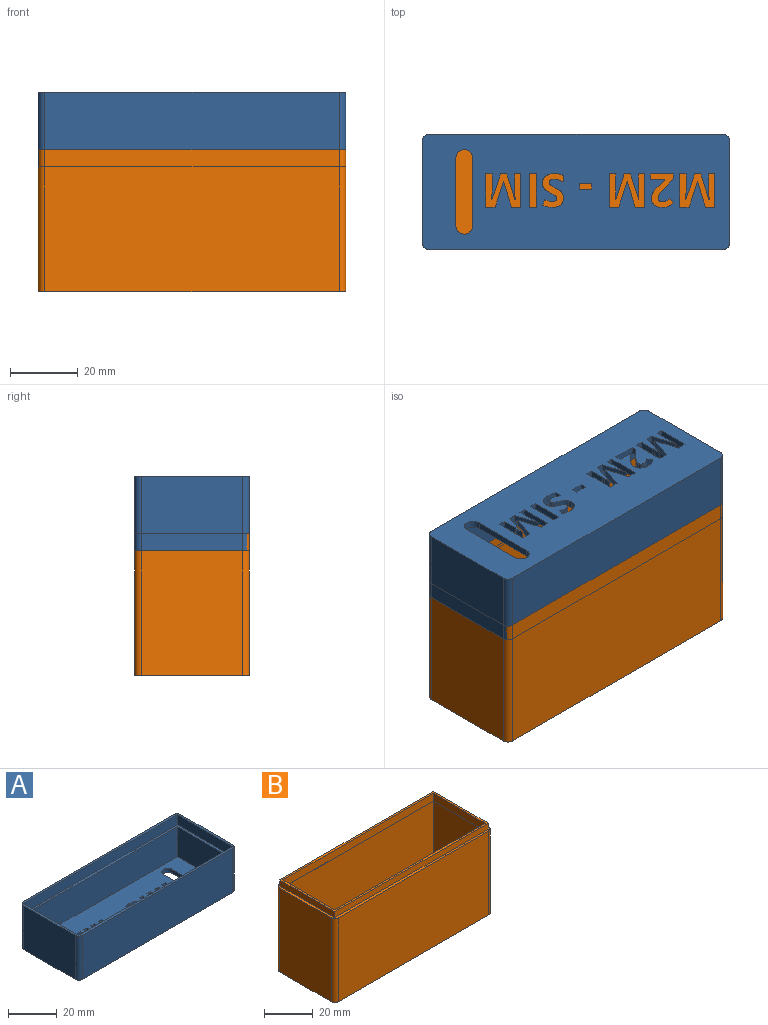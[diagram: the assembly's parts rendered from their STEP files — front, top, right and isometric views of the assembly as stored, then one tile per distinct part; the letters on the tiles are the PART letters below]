
ASSEMBLY  parts=2 mates=1
PART A: 141 faces, bbox 91x34x22 mm
  f0: plane 91x34mm, normal (0,0,-1), area 2673.6mm2, adj f3,f4,f5,f6,f16,f17,f18,f19
  f1: plane 87x30mm, normal (0,0,1), area 2193.1mm2, adj f12,f13,f14,f15,f16,f17,f18,f19
  f2: plane 91x34mm, normal (0,0,1), area 242.6mm2, adj f3,f4,f5,f6,f7,f8,f9,f10
  f3: plane 87x22mm, normal (0,-1,0), area 1914mm2, adj f0,f2,f20,f23
  f4: plane 30x22mm, normal (1,0,0), area 660mm2, adj f0,f2,f20,f21
  f5: plane 87x22mm, normal (0,1,0), area 1914mm2, adj f0,f2,f21,f22
  f6: plane 30x22mm, normal (-1,0,0), area 660mm2, adj f0,f2,f22,f23
  f7: plane 32x5mm, normal (1,0,0), area 160mm2, adj f2,f8,f10,f11
  f8: plane 89x5mm, normal (0,1,0), area 445mm2, adj f2,f7,f9,f11
  f9: plane 32x5mm, normal (-1,0,0), area 160mm2, adj f2,f8,f10,f11
  f10: plane 89x5mm, normal (0,-1,0), area 445mm2, adj f2,f7,f9,f11
  f11: plane 89x32mm, normal (0,0,1), area 238mm2, adj f7,f8,f9,f10,f12,f13,f14,f15
  f12: plane 30x15mm, normal (1,0,0), area 450mm2, adj f1,f11,f13,f15
  f13: plane 87x15mm, normal (0,-1,0), area 1305mm2, adj f1,f11,f12,f14
  f14: plane 30x15mm, normal (-1,0,0), area 450mm2, adj f1,f11,f13,f15
  f15: plane 87x15mm, normal (0,1,0), area 1305mm2, adj f1,f11,f12,f14
  f16: cylinder r=2.5mm len=5mm, axis (0,0,1), area 15.7mm2, adj f0,f1,f17,f19
  f17: plane 20x2mm, normal (-1,0,0), area 40mm2, adj f0,f1,f16,f18
  f18: cylinder r=2.5mm len=5mm, axis (0,0,1), area 15.7mm2, adj f0,f1,f17,f19
  f19: plane 20x2mm, normal (1,0,0), area 40mm2, adj f0,f1,f16,f18
  f20: cylinder r=2mm len=22mm, axis (0,0,-1), area 69.1mm2, adj f0,f2,f3,f4
  f21: cylinder r=2mm len=22mm, axis (0,0,1), area 69.1mm2, adj f0,f2,f4,f5
  f22: cylinder r=2mm len=22mm, axis (0,0,-1), area 69.1mm2, adj f0,f2,f5,f6
  f23: cylinder r=2mm len=22mm, axis (0,0,1), area 69.1mm2, adj f0,f2,f3,f6
  f24: plane 2x1.91mm, normal (0,-1,0), area 3.8mm2, adj f0,f1,f25,f42
  f25: plane 7.68x2.53mm, normal (-0.95,-0.31,0), area 16.2mm2, adj f0,f1,f24,f26
  f26: plane 2x0.06mm, normal (0,-1,0), area 0.1mm2, adj f0,f1,f25,f27
  f27: extruded ~2.28x2mm, area 4.6mm2, adj f0,f1,f26,f28
  f28: extruded ~2x0.76mm, area 1.5mm2, adj f0,f1,f27,f29
  f29: plane 4.64x2mm, normal (1,0,0), area 9.3mm2, adj f0,f1,f28,f30
  f30: plane 2x1.94mm, normal (0,-1,0), area 3.9mm2, adj f0,f1,f29,f31
  f31: plane 9.8x2mm, normal (-1,0,0), area 19.6mm2, adj f0,f1,f30,f32
  f32: plane 2.83x2mm, normal (0,1,0), area 5.7mm2, adj f0,f1,f31,f33
  f33: plane 7.5x2.46mm, normal (0.95,0.31,0), area 15.8mm2, adj f0,f1,f32,f34
  f34: plane 2x0.04mm, normal (0,1,0), area 0.1mm2, adj f0,f1,f33,f35
  f35: plane 7.5x2.32mm, normal (-0.96,0.3,0), area 15.7mm2, adj f0,f1,f34,f36
  f36: plane 2.83x2mm, normal (0,1,0), area 5.7mm2, adj f0,f1,f35,f37
  f37: plane 9.8x2mm, normal (1,0,0), area 19.6mm2, adj f0,f1,f36,f38
  f38: plane 2x1.86mm, normal (0,-1,0), area 3.7mm2, adj f0,f1,f37,f39
  f39: plane 4.56x2mm, normal (-1,0,0), area 9.1mm2, adj f0,f1,f38,f40
  f40: extruded ~3.13x2mm, area 6.3mm2, adj f0,f1,f39,f41
  f41: plane 2x0.06mm, normal (0,-1,0), area 0.1mm2, adj f0,f1,f40,f42
  f42: plane 7.69x2.36mm, normal (0.96,-0.29,0), area 16.1mm2, adj f0,f1,f24,f41
  f43: plane 2.08x2mm, normal (0,-1,0), area 4.2mm2, adj f0,f1,f44,f46
  f44: plane 9.8x2mm, normal (-1,0,0), area 19.6mm2, adj f0,f1,f43,f45
  f45: plane 2.08x2mm, normal (0,1,0), area 4.2mm2, adj f0,f1,f44,f46
  f46: plane 9.8x2mm, normal (1,0,0), area 19.6mm2, adj f0,f1,f43,f45
  f47: extruded ~2x1.62mm, area 3.5mm2, adj f0,f1,f48,f74
  f48: extruded ~2x1.89mm, area 4.6mm2, adj f0,f1,f47,f49
  f49: extruded ~2x1.32mm, area 3mm2, adj f0,f1,f48,f50
  f50: extruded ~2x0.41mm, area 1.1mm2, adj f0,f1,f49,f51
  f51: extruded ~2x0.48mm, area 1mm2, adj f0,f1,f50,f52
  f52: extruded ~2x0.72mm, area 1.6mm2, adj f0,f1,f51,f53
  f53: extruded ~2x0.91mm, area 1.9mm2, adj f0,f1,f52,f54
  f54: extruded ~2x1.01mm, area 2mm2, adj f0,f1,f53,f55
  f55: extruded ~2x1.3mm, area 2.7mm2, adj f0,f1,f54,f56
  f56: plane 2x1.62mm, normal (-0.92,-0.38,0), area 3.5mm2, adj f0,f1,f55,f57
  f57: extruded ~2x1.45mm, area 3.1mm2, adj f0,f1,f56,f58
  f58: extruded ~2x1.46mm, area 2.9mm2, adj f0,f1,f57,f59
  f59: extruded ~2.44x2mm, area 5.2mm2, adj f0,f1,f58,f60
  f60: extruded ~2.05x2mm, area 4.6mm2, adj f0,f1,f59,f61
  f61: extruded ~2x1.21mm, area 2.5mm2, adj f0,f1,f60,f62
  f62: extruded ~2x0.91mm, area 2.3mm2, adj f0,f1,f61,f63
  f63: extruded ~2x1.35mm, area 3.2mm2, adj f0,f1,f62,f64
  f64: extruded ~2x1.27mm, area 2.9mm2, adj f0,f1,f63,f65
  f65: extruded ~2x0.47mm, area 1.3mm2, adj f0,f1,f64,f66
  f66: extruded ~2x0.51mm, area 1.1mm2, adj f0,f1,f65,f67
  f67: extruded ~2x0.78mm, area 1.8mm2, adj f0,f1,f66,f68
  f68: extruded ~2x1.05mm, area 2.2mm2, adj f0,f1,f67,f69
  f69: extruded ~2x1.26mm, area 2.5mm2, adj f0,f1,f68,f70
  f70: extruded ~2x1.68mm, area 3.6mm2, adj f0,f1,f69,f71
  f71: plane 2x1.93mm, normal (1,0,0), area 3.9mm2, adj f0,f1,f70,f72
  f72: extruded ~2.78x2mm, area 5.7mm2, adj f0,f1,f71,f73
  f73: extruded ~2.66x2mm, area 5.6mm2, adj f0,f1,f72,f74
  f74: extruded ~2.09x2mm, area 4.8mm2, adj f0,f1,f47,f73
  f75: plane 3.6x2mm, normal (0,-1,0), area 7.2mm2, adj f0,f1,f76,f78
  f76: plane 2x1.68mm, normal (-1,0,0), area 3.4mm2, adj f0,f1,f75,f77
  f77: plane 3.6x2mm, normal (0,1,0), area 7.2mm2, adj f0,f1,f76,f78
  f78: plane 2x1.68mm, normal (1,0,0), area 3.4mm2, adj f0,f1,f75,f77
  f79: plane 2x1.91mm, normal (0,-1,0), area 3.8mm2, adj f0,f1,f80,f97
  f80: plane 7.68x2.53mm, normal (-0.95,-0.31,0), area 16.2mm2, adj f0,f1,f79,f81
  f81: plane 2x0.06mm, normal (0,-1,0), area 0.1mm2, adj f0,f1,f80,f82
  f82: extruded ~2.28x2mm, area 4.6mm2, adj f0,f1,f81,f83
  f83: extruded ~2x0.76mm, area 1.5mm2, adj f0,f1,f82,f84
  f84: plane 4.64x2mm, normal (1,0,0), area 9.3mm2, adj f0,f1,f83,f85
  f85: plane 2x1.94mm, normal (0,-1,0), area 3.9mm2, adj f0,f1,f84,f86
  f86: plane 9.8x2mm, normal (-1,0,0), area 19.6mm2, adj f0,f1,f85,f87
  f87: plane 2.83x2mm, normal (0,1,0), area 5.7mm2, adj f0,f1,f86,f88
  f88: plane 7.5x2.46mm, normal (0.95,0.31,0), area 15.8mm2, adj f0,f1,f87,f89
  f89: plane 2x0.04mm, normal (0,1,0), area 0.1mm2, adj f0,f1,f88,f90
  f90: plane 7.5x2.32mm, normal (-0.96,0.3,0), area 15.7mm2, adj f0,f1,f89,f91
  f91: plane 2.83x2mm, normal (0,1,0), area 5.7mm2, adj f0,f1,f90,f92
  f92: plane 9.8x2mm, normal (1,0,0), area 19.6mm2, adj f0,f1,f91,f93
  f93: plane 2x1.86mm, normal (0,-1,0), area 3.7mm2, adj f0,f1,f92,f94
  f94: plane 4.56x2mm, normal (-1,0,0), area 9.1mm2, adj f0,f1,f93,f95
  f95: extruded ~3.13x2mm, area 6.3mm2, adj f0,f1,f94,f96
  f96: plane 2x0.06mm, normal (0,-1,0), area 0.1mm2, adj f0,f1,f95,f97
  f97: plane 7.69x2.36mm, normal (0.96,-0.29,0), area 16.1mm2, adj f0,f1,f79,f96
  f98: plane 2x1.74mm, normal (-1,0,0), area 3.5mm2, adj f0,f1,f99,f121
  f99: plane 4.27x2mm, normal (0,1,0), area 8.5mm2, adj f0,f1,f98,f100
  f100: plane 2x0.09mm, normal (-1,0,0), area 0.2mm2, adj f0,f1,f99,f101
  f101: plane 2x1.26mm, normal (-0.69,-0.73,0), area 3.5mm2, adj f0,f1,f100,f102
  f102: extruded ~2x1.78mm, area 5mm2, adj f0,f1,f101,f103
  f103: extruded ~2x1.22mm, area 2.9mm2, adj f0,f1,f102,f104
  f104: extruded ~2x1.27mm, area 2.6mm2, adj f0,f1,f103,f105
  f105: extruded ~2x1.38mm, area 2.9mm2, adj f0,f1,f104,f106
  f106: extruded ~2x1.09mm, area 2.9mm2, adj f0,f1,f105,f107
  f107: extruded ~2x1.62mm, area 3.3mm2, adj f0,f1,f106,f108
  f108: extruded ~2x1.26mm, area 2.5mm2, adj f0,f1,f107,f109
  f109: extruded ~2x1.04mm, area 2.2mm2, adj f0,f1,f108,f110
  f110: extruded ~2x1.2mm, area 3mm2, adj f0,f1,f109,f111
  f111: plane 2x1.33mm, normal (0.76,-0.65,0), area 3.5mm2, adj f0,f1,f110,f112
  f112: extruded ~2x1.12mm, area 2.7mm2, adj f0,f1,f111,f113
  f113: extruded ~2x1.11mm, area 2.3mm2, adj f0,f1,f112,f114
  f114: extruded ~2x0.87mm, area 1.9mm2, adj f0,f1,f113,f115
  f115: extruded ~2x0.88mm, area 1.9mm2, adj f0,f1,f114,f116
  f116: extruded ~2x0.76mm, area 1.6mm2, adj f0,f1,f115,f117
  f117: extruded ~2x0.8mm, area 1.9mm2, adj f0,f1,f116,f118
  f118: extruded ~2x1.55mm, area 4.2mm2, adj f0,f1,f117,f119
  f119: plane 2.49x2.46mm, normal (0.71,0.7,0), area 7mm2, adj f0,f1,f118,f120
  f120: plane 2x1.44mm, normal (1,0,0), area 2.9mm2, adj f0,f1,f119,f121
  f121: plane 6.85x2mm, normal (0,-1,0), area 13.7mm2, adj f0,f1,f98,f120
  f122: plane 2x1.91mm, normal (0,-1,0), area 3.8mm2, adj f0,f1,f123,f140
  f123: plane 7.68x2.53mm, normal (-0.95,-0.31,0), area 16.2mm2, adj f0,f1,f122,f124
  f124: plane 2x0.06mm, normal (0,-1,0), area 0.1mm2, adj f0,f1,f123,f125
  f125: extruded ~2.28x2mm, area 4.6mm2, adj f0,f1,f124,f126
  f126: extruded ~2x0.76mm, area 1.5mm2, adj f0,f1,f125,f127
  f127: plane 4.64x2mm, normal (1,0,0), area 9.3mm2, adj f0,f1,f126,f128
  f128: plane 2x1.94mm, normal (0,-1,0), area 3.9mm2, adj f0,f1,f127,f129
  f129: plane 9.8x2mm, normal (-1,0,0), area 19.6mm2, adj f0,f1,f128,f130
  f130: plane 2.83x2mm, normal (0,1,0), area 5.7mm2, adj f0,f1,f129,f131
  f131: plane 7.5x2.46mm, normal (0.95,0.31,0), area 15.8mm2, adj f0,f1,f130,f132
  f132: plane 2x0.04mm, normal (0,1,0), area 0.1mm2, adj f0,f1,f131,f133
  f133: plane 7.5x2.32mm, normal (-0.96,0.3,0), area 15.7mm2, adj f0,f1,f132,f134
  f134: plane 2.83x2mm, normal (0,1,0), area 5.7mm2, adj f0,f1,f133,f135
  f135: plane 9.8x2mm, normal (1,0,0), area 19.6mm2, adj f0,f1,f134,f136
  f136: plane 2x1.86mm, normal (0,-1,0), area 3.7mm2, adj f0,f1,f135,f137
  f137: plane 4.56x2mm, normal (-1,0,0), area 9.1mm2, adj f0,f1,f136,f138
  f138: extruded ~3.13x2mm, area 6.3mm2, adj f0,f1,f137,f139
  f139: plane 2x0.06mm, normal (0,-1,0), area 0.1mm2, adj f0,f1,f138,f140
  f140: plane 7.69x2.36mm, normal (0.96,-0.29,0), area 16.1mm2, adj f0,f1,f122,f139
PART B: 25 faces, bbox 91x34x45 mm
  f0: plane 91x34mm, normal (0,0,1), area 270.1mm2, adj f1,f2,f3,f4,f8,f9,f10,f11
  f1: plane 87x42mm, normal (0,-1,0), area 3654mm2, adj f0,f5,f21,f24
  f2: plane 42x30mm, normal (1,0,0), area 1260mm2, adj f0,f5,f21,f22
  f3: plane 87x42mm, normal (0,1,0), area 3654mm2, adj f0,f5,f22,f23
  f4: plane 42x30mm, normal (-1,0,0), area 1260mm2, adj f0,f5,f23,f24
  f5: plane 91x34mm, normal (0,0,-1), area 3090.6mm2, adj f1,f2,f3,f4,f21,f22,f23,f24
  f6: plane 87x30mm, normal (0,0,-1), area 3.2mm2, adj f12,f13,f14,f15,f17,f18,f19,f20
  f7: plane 88.75x31.78mm, normal (0,0,1), area 213.7mm2, adj f8,f9,f10,f11,f12,f13,f14,f15
  f8: plane 88.75x3mm, normal (0,-1,0), area 266.2mm2, adj f0,f7,f9,f11
  f9: plane 31.78x3mm, normal (1,0,0), area 95.3mm2, adj f0,f7,f8,f10
  f10: plane 88.75x3mm, normal (0,1,0), area 266.2mm2, adj f0,f7,f9,f11
  f11: plane 31.78x3mm, normal (-1,0,0), area 95.3mm2, adj f0,f7,f8,f10
  f12: plane 86.95x3.9mm, normal (0,1,0), area 339.1mm2, adj f6,f7,f13,f15
  f13: plane 29.98x3.9mm, normal (-1,0,0), area 116.9mm2, adj f6,f7,f12,f14
  f14: plane 86.95x3.9mm, normal (0,-1,0), area 339.1mm2, adj f6,f7,f13,f15
  f15: plane 29.98x3.9mm, normal (1,0,0), area 116.9mm2, adj f6,f7,f12,f14
  f16: plane 87x30mm, normal (0,0,1), area 2610mm2, adj f17,f18,f19,f20
  f17: plane 39.1x30mm, normal (1,0,0), area 1173mm2, adj f6,f16,f18,f20
  f18: plane 87x39.1mm, normal (0,-1,0), area 3401.7mm2, adj f6,f16,f17,f19
  f19: plane 39.1x30mm, normal (-1,0,0), area 1173mm2, adj f6,f16,f18,f20
  f20: plane 87x39.1mm, normal (0,1,0), area 3401.7mm2, adj f6,f16,f17,f19
  f21: cylinder r=2mm len=42mm, axis (0,0,-1), area 131.9mm2, adj f0,f1,f2,f5
  f22: cylinder r=2mm len=42mm, axis (0,0,1), area 131.9mm2, adj f0,f2,f3,f5
  f23: cylinder r=2mm len=42mm, axis (0,0,-1), area 131.9mm2, adj f0,f3,f4,f5
  f24: cylinder r=2mm len=42mm, axis (0,0,1), area 131.9mm2, adj f0,f1,f4,f5
PLACE A rot(axis=(0,1,0),180deg) t=(-22.83,-4.47,46.56)mm
PLACE B t=(-22.83,-4.47,-8.44)mm
MATE parallel A.f11 <-> B.f0  axis (0,0,-1) through (-22.83,-4.47,31.56)mm
